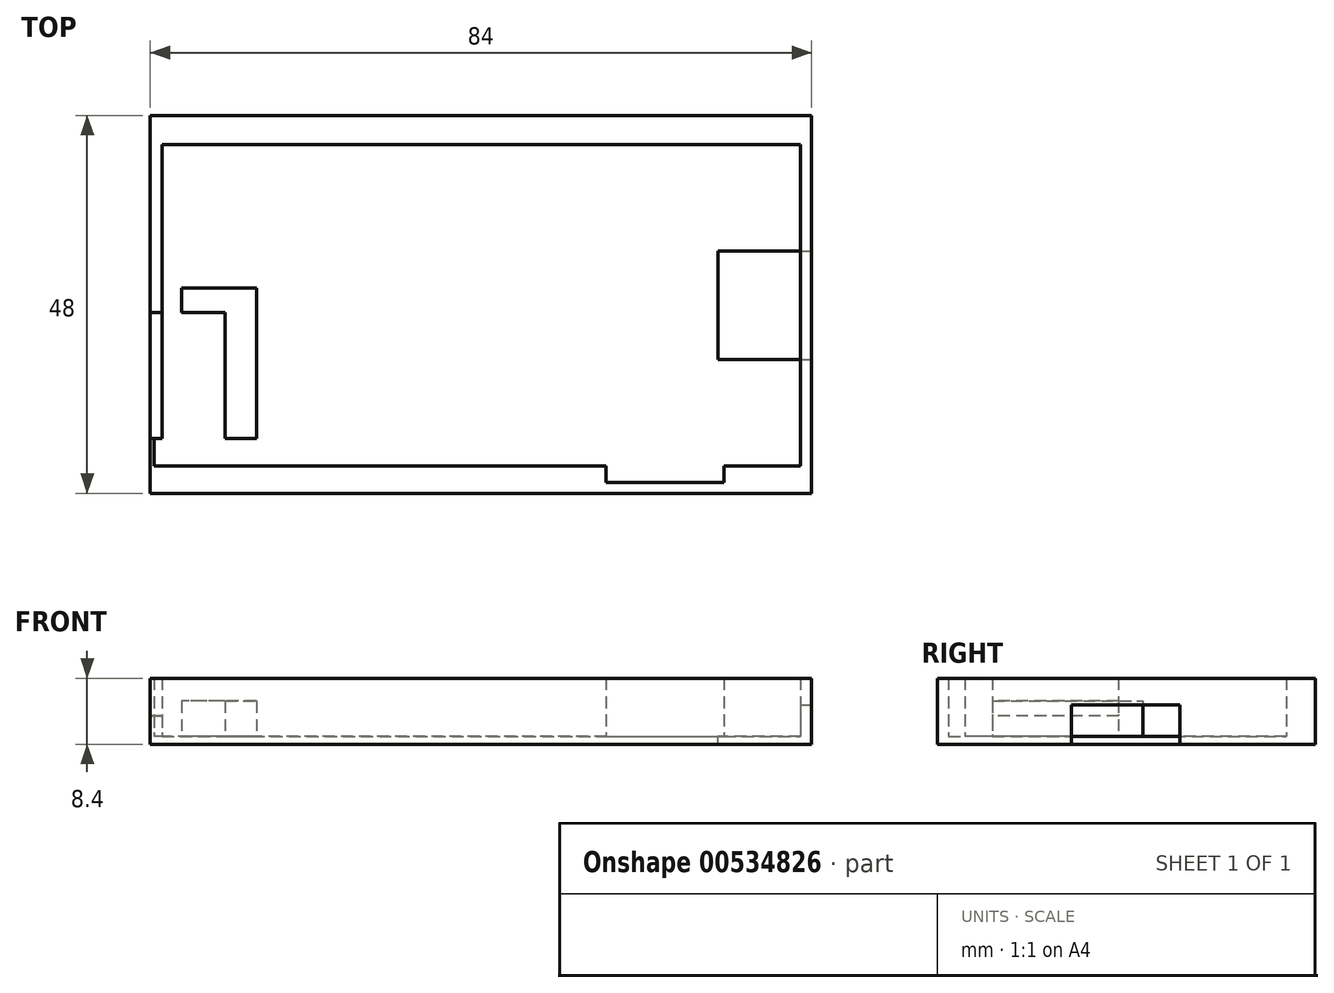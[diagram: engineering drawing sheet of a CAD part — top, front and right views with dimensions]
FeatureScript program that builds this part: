
annotation { "Feature Type Name" : "Feature", "Feature Type Description" : "" }
export const myFeature = defineFeature(function(context is Context, id is Id, definition is map)
    precondition{}
    {
        {
            var Q0;
            Q0=qCreatedBy(makeId("Top.planeOp"),FACE);
            var sketch = newSketch(context, id + "F0", { "sketchPlane" : qUnion([Q0])});
            skLineSegment(sketch, "E0.0", {"start": v(-50.68, -41.57) * mm, "end": v(30.32, -41.57) * mm});
            skLineSegment(sketch, "E1.0", {"start": v(-50.68, 6.43) * mm, "end": v(30.32, 6.43) * mm});
            skLineSegment(sketch, "E2", {"start": v(-50.68, -1.57) * mm, "end": v(-50.68, 6.43) * mm});
            skLineSegment(sketch, "E3", {"start": v(-50.68, 6.43) * mm, "end": v(-50.68, 6.43) * mm});
            skLineSegment(sketch, "E4", {"start": v(-50.68, -41.57) * mm, "end": v(-50.68, -41.57) * mm});
            skLineSegment(sketch, "E5", {"start": v(-50.68, -35.57) * mm, "end": v(-50.68, -41.57) * mm});
            skLineSegment(sketch, "E6", {"start": v(30.32, -41.57) * mm, "end": v(33.32, -41.57) * mm});
            skLineSegment(sketch, "E7", {"start": v(30.32, 6.43) * mm, "end": v(33.32, 6.43) * mm});
            skLineSegment(sketch, "E8", {"start": v(9.72, -37.67) * mm, "end": v(19.72, -37.67) * mm});
            skLineSegment(sketch, "E9", {"start": v(19.72, -37.67) * mm, "end": v(19.72, -35.57) * mm});
            skLineSegment(sketch, "E10", {"start": v(9.72, -37.67) * mm, "end": v(9.72, -35.67) * mm});
            skLineSegment(sketch, "E11", {"start": v(29.42, -34.57) * mm, "end": v(33.32, -34.57) * mm});
            skLineSegment(sketch, "E12", {"start": v(29.42, -26.07) * mm, "end": v(33.32, -26.07) * mm});
            skLineSegment(sketch, "E13", {"start": v(-46.68, -34.57) * mm, "end": v(-50.68, -34.57) * mm});
            skLineSegment(sketch, "E14", {"start": v(-50.68, -18.57) * mm, "end": v(-46.68, -18.57) * mm});
            skLineSegment(sketch, "E15", {"start": v(-46.68, 0.23) * mm, "end": v(29.42, 0.23) * mm});
            skLineSegment(sketch, "E16", {"start": v(-50.68, -18.57) * mm, "end": v(-50.68, 6.43) * mm});
            skLineSegment(sketch, "E17", {"start": v(-50.68, -34.57) * mm, "end": v(-50.68, -41.57) * mm});
            skLineSegment(sketch, "E18", {"start": v(33.32, 6.43) * mm, "end": v(33.32, -26.07) * mm});
            skLineSegment(sketch, "E19", {"start": v(33.32, -34.57) * mm, "end": v(33.32, -41.57) * mm});
            skLineSegment(sketch, "E20", {"start": v(29.42, -34.57) * mm, "end": v(29.42, -35.57) * mm});
            skLineSegment(sketch, "E21", {"start": v(-46.68, -34.57) * mm, "end": v(-46.68, -35.67) * mm});
            skLineSegment(sketch, "E22", {"start": v(-46.68, -18.57) * mm, "end": v(-46.68, 0.23) * mm});
            skLineSegment(sketch, "E23", {"start": v(29.42, 0.23) * mm, "end": v(29.42, -26.07) * mm});
            skLineSegment(sketch, "E24.0", {"start": v(31.92, 2.73) * mm, "end": v(31.92, -25.77) * mm});
            skLineSegment(sketch, "E24.1", {"start": v(-49.18, 2.73) * mm, "end": v(31.92, 2.73) * mm});
            skLineSegment(sketch, "E24.2", {"start": v(-49.18, -18.57) * mm, "end": v(-49.18, 2.73) * mm});
            skLineSegment(sketch, "E25", {"start": v(29.42, -35.57) * mm, "end": v(19.72, -35.57) * mm});
            skLineSegment(sketch, "E26", {"start": v(9.72, -35.67) * mm, "end": v(-46.68, -35.67) * mm});
            skLineSegment(sketch, "E27.0", {"start": v(29.42, -38.07) * mm, "end": v(22.22, -38.07) * mm});
            skLineSegment(sketch, "E27.1", {"start": v(7.22, -38.07) * mm, "end": v(-46.68, -38.07) * mm});
            skLineSegment(sketch, "E27.2", {"start": v(7.22, -40.17) * mm, "end": v(7.22, -38.07) * mm});
            skLineSegment(sketch, "E27.3", {"start": v(7.22, -40.17) * mm, "end": v(22.22, -40.17) * mm});
            skLineSegment(sketch, "E27.4", {"start": v(22.22, -40.17) * mm, "end": v(22.22, -38.07) * mm});
            skLineSegment(sketch, "E28", {"start": v(29.42, -38.07) * mm, "end": v(33.32, -38.07) * mm});
            skLineSegment(sketch, "E29", {"start": v(-46.68, -38.07) * mm, "end": v(-50.68, -38.07) * mm});
            skLineSegment(sketch, "E30", {"start": v(33.32, 6.43) * mm, "end": v(33.32, -41.57) * mm});
            skLineSegment(sketch, "E31", {"start": v(-50.68, 6.43) * mm, "end": v(-50.68, -41.57) * mm});
            skLineSegment(sketch, "E32", {"start": v(29.42, -24.57) * mm, "end": v(21.42, -24.57) * mm});
            skLineSegment(sketch, "E33", {"start": v(29.42, -12.77) * mm, "end": v(21.42, -12.77) * mm});
            skLineSegment(sketch, "E34", {"start": v(21.42, -12.77) * mm, "end": v(21.42, -24.57) * mm});
            skLineSegment(sketch, "E35", {"start": v(59.8, 40.02) * mm, "end": v(59.8, -75.73) * mm});
            skLineSegment(sketch, "E36", {"start": v(31.92, -25.77) * mm, "end": v(31.92, -34.57) * mm});
            skPoint(sketch, "E36.endSnap0", {"position": v(31.37, -34.57) * mm});
            skLineSegment(sketch, "E37", {"start": v(31.92, -34.57) * mm, "end": v(31.92, -38.07) * mm});
            skLineSegment(sketch, "E38", {"start": v(-46.68, -35.67) * mm, "end": v(-46.68, -38.07) * mm});
            skLineSegment(sketch, "E39", {"start": v(-50.18, -34.57) * mm, "end": v(-50.18, -38.07) * mm});
            skLineSegment(sketch, "E40", {"start": v(-49.18, -18.57) * mm, "end": v(-49.18, -34.57) * mm});
            skLineSegment(sketch, "E41", {"start": v(-41.18, -18.57) * mm, "end": v(-41.18, -34.57) * mm});
            skLineSegment(sketch, "E42", {"start": v(-37.18, -34.57) * mm, "end": v(-37.18, -18.57) * mm});
            skLineSegment(sketch, "E43", {"start": v(-41.18, -18.57) * mm, "end": v(-37.18, -18.57) * mm});
            skLineSegment(sketch, "E44", {"start": v(-41.18, -34.57) * mm, "end": v(-37.18, -34.57) * mm});
            skLineSegment(sketch, "E45", {"start": v(-37.18, -18.57) * mm, "end": v(-37.18, -15.51) * mm});
            skLineSegment(sketch, "E46", {"start": v(-37.18, -15.51) * mm, "end": v(-46.68, -15.51) * mm});
            skLineSegment(sketch, "E47", {"start": v(-41.18, -18.57) * mm, "end": v(-46.68, -18.57) * mm});
            skLineSegment(sketch, "E48", {"start": v(29.42, -24.57) * mm, "end": v(33.32, -24.57) * mm});
            skLineSegment(sketch, "E49", {"start": v(29.42, -12.77) * mm, "end": v(33.32, -12.77) * mm});
            skLineSegment(sketch, "E50", {"start": v(29.42, -10.77) * mm, "end": v(21.42, -10.77) * mm});
            skLineSegment(sketch, "E51", {"start": v(21.42, -10.77) * mm, "end": v(21.42, -12.77) * mm});
            skLineSegment(sketch, "E52", {"start": v(29.42, -10.77) * mm, "end": v(33.32, -10.77) * mm});
            skSolve(sketch);
        }
        {
            var Q0;
            Q0=makeQuery(id+"F0.imprint","IMPRINT",FACE,{"disambiguationData":[TD([[makeQuery(id+"F0.imprint","IMPRINT",EDGE,{"derivedFrom":sQuery(id+"F0.wireOp",EDGE,"E8")}),1.0]])]});
            var Q1;
            Q1=makeQuery(id+"F0.imprint","IMPRINT",FACE,{"disambiguationData":[TD([[makeQuery(id+"F0.imprint","IMPRINT",EDGE,{"derivedFrom":sQuery(id+"F0.wireOp",EDGE,"E15")}),1.0]])]});
            var Q2;
            {var subQ9=sQuery(id+"F0.wireOp",EDGE,"E1.0");Q2=makeQuery(id+"F0.imprint","IMPRINT",FACE,{"disambiguationData":[TD([[makeQuery(id+"F0.imprint","IMPRINT",EDGE,{"derivedFrom":subQ9}),-1.0]])]});}
            var Q3;
            Q3=makeQuery(id+"F0.imprint","IMPRINT",FACE,{"disambiguationData":[TD([[makeQuery(id+"F0.imprint","IMPRINT",EDGE,{"derivedFrom":sQuery(id+"F0.wireOp",EDGE,"E8")}),-1.0]])]});
            var Q4;
            {var subQ4=sQuery(id+"F0.wireOp",EDGE,"E0.0");Q4=makeQuery(id+"F0.imprint","IMPRINT",FACE,{"disambiguationData":[TD([[makeQuery(id+"F0.imprint","IMPRINT",EDGE,{"derivedFrom":subQ4}),1.0]])]});}
            var Q5;
            {var subQ3=sQuery(id+"F0.wireOp",EDGE,"E36");Q5=makeQuery(id+"F0.imprint","IMPRINT",FACE,{"disambiguationData":[TD([[makeQuery(id+"F0.imprint","IMPRINT",EDGE,{"derivedFrom":subQ3}),1.0]])]});}
            var Q6;
            {var subQ3=sQuery(id+"F0.wireOp",EDGE,"E37");Q6=makeQuery(id+"F0.imprint","IMPRINT",FACE,{"disambiguationData":[TD([[makeQuery(id+"F0.imprint","IMPRINT",EDGE,{"derivedFrom":subQ3}),1.0]])]});}
            var Q7;
            {var subQ0=sQuery(id+"F0.wireOp",EDGE,"E13");Q7=makeQuery(id+"F0.imprint","IMPRINT",FACE,{"disambiguationData":[TD([[makeQuery(id+"F0.imprint","IMPRINT",EDGE,{"derivedFrom":subQ0}),-1.0]])]});}
            var Q8;
            {var subQ2=sQuery(id+"F0.wireOp",EDGE,"E13");Q8=makeQuery(id+"F0.imprint","IMPRINT",FACE,{"disambiguationData":[TD([[makeQuery(id+"F0.imprint","IMPRINT",EDGE,{"derivedFrom":subQ2}),1.0]])]});}
            var Q9;
            {var subQ3=sQuery(id+"F0.wireOp",EDGE,"E21");Q9=makeQuery(id+"F0.imprint","IMPRINT",FACE,{"disambiguationData":[TD([[makeQuery(id+"F0.imprint","IMPRINT",EDGE,{"derivedFrom":subQ3}),-1.0]])]});}
            var Q10;
            {var subQ3=sQuery(id+"F0.wireOp",EDGE,"E39");Q10=makeQuery(id+"F0.imprint","IMPRINT",FACE,{"disambiguationData":[TD([[makeQuery(id+"F0.imprint","IMPRINT",EDGE,{"derivedFrom":subQ3}),-1.0]])]});}
            var Q11;
            Q11=makeQuery(id+"F0.imprint","IMPRINT",FACE,{"disambiguationData":[TD([[makeQuery(id+"F0.imprint","IMPRINT",EDGE,{"derivedFrom":sQuery(id+"F0.wireOp",EDGE,"E41")}),1.0]])]});
            var Q12;
            Q12=makeQuery(id+"F0.imprint","IMPRINT",FACE,{"disambiguationData":[TD([[makeQuery(id+"F0.imprint","IMPRINT",EDGE,{"derivedFrom":sQuery(id+"F0.wireOp",EDGE,"E43")}),1.0]])]});
            var Q13;
            {var subQ0=sQuery(id+"F0.wireOp",EDGE,"E30");var subQ1=sQuery(id+"F0.wireOp",EDGE,"E12");var subQ2=makeQuery(id+"F0.imprint","INTERSECT",VERTEX,{"derivedFrom":[subQ1,subQ0]});Q13=makeQuery(id+"F0.imprint","IMPRINT",FACE,{"disambiguationData":[TD([[makeQuery(id+"F0.imprint","IMPRINT",EDGE,{"disambiguationData":[TD([[subQ2,1.0]])],"derivedFrom":subQ0}),-1.0]])]});}
            var Q14;
            {var subQ0=sQuery(id+"F0.wireOp",EDGE,"E23");var subQ1=sQuery(id+"F0.wireOp",EDGE,"E12");var subQ2=makeQuery(id+"F0.imprint","INTERSECT",VERTEX,{"derivedFrom":[subQ1,subQ0]});Q14=makeQuery(id+"F0.imprint","IMPRINT",FACE,{"disambiguationData":[TD([[makeQuery(id+"F0.imprint","IMPRINT",EDGE,{"disambiguationData":[TD([[subQ2,-1.0]])],"derivedFrom":subQ1}),1.0]])]});}
            var Q15;
            {var subQ4=sQuery(id+"F0.wireOp",EDGE,"E20");Q15=makeQuery(id+"F0.imprint","IMPRINT",FACE,{"disambiguationData":[TD([[makeQuery(id+"F0.imprint","IMPRINT",EDGE,{"derivedFrom":subQ4}),-1.0]])]});}
            var Q16;
            {var subQ8=sQuery(id+"F0.wireOp",EDGE,"E24.2");Q16=makeQuery(id+"F0.imprint","IMPRINT",FACE,{"disambiguationData":[TD([[makeQuery(id+"F0.imprint","IMPRINT",EDGE,{"derivedFrom":subQ8}),-1.0]])]});}
            extrude(context, id + "F1", {"entities" : qUnion([Q0, Q1, Q2, Q3, Q4, Q5, Q6, Q7, Q8, Q9, Q10, Q11, Q12, Q13, Q14, Q15, Q16]), "oppositeDirection" : true, "depth" : 1 * mm, "offsetDistance" : 25 * mm});
        }
        {
            var Q0;
            {var subQ3=sQuery(id+"F0.wireOp",EDGE,"KbTD920z-0UKZ-KzV2-GkzX-uQvUb1giLStP");Q0=makeQuery(id+"F0.imprint","IMPRINT",FACE,{"disambiguationData":[TD([[makeQuery(id+"F0.imprint","IMPRINT",EDGE,{"derivedFrom":subQ3}),1.0]])]});}
            var Q1;
            {var subQ5=sQuery(id+"F0.wireOp",EDGE,"E0.0");Q1=makeQuery(id+"F0.imprint","IMPRINT",FACE,{"disambiguationData":[TD([[makeQuery(id+"F0.imprint","IMPRINT",EDGE,{"derivedFrom":subQ5}),1.0]])]});}
            var Q2;
            {var subQ9=sQuery(id+"F0.wireOp",EDGE,"E1.0");Q2=makeQuery(id+"F0.imprint","IMPRINT",FACE,{"disambiguationData":[TD([[makeQuery(id+"F0.imprint","IMPRINT",EDGE,{"derivedFrom":subQ9}),-1.0]])]});}
            var Q3;
            {var subQ3=sQuery(id+"F0.wireOp",EDGE,"E36");Q3=makeQuery(id+"F0.imprint","IMPRINT",FACE,{"disambiguationData":[TD([[makeQuery(id+"F0.imprint","IMPRINT",EDGE,{"derivedFrom":subQ3}),1.0]])]});}
            var Q4;
            {var subQ1=sQuery(id+"F0.wireOp",EDGE,"E19");Q4=makeQuery(id+"F0.imprint","IMPRINT",FACE,{"disambiguationData":[TD([[makeQuery(id+"F0.imprint","IMPRINT",EDGE,{"derivedFrom":subQ1}),-1.0]])]});}
            var Q5;
            {var subQ3=sQuery(id+"F0.wireOp",EDGE,"E39");Q5=makeQuery(id+"F0.imprint","IMPRINT",FACE,{"disambiguationData":[TD([[makeQuery(id+"F0.imprint","IMPRINT",EDGE,{"derivedFrom":subQ3}),-1.0]])]});}
            var Q6;
            {var subQ0=sQuery(id+"F0.wireOp",EDGE,"E30");var subQ1=sQuery(id+"F0.wireOp",EDGE,"E12");var subQ2=makeQuery(id+"F0.imprint","INTERSECT",VERTEX,{"derivedFrom":[subQ1,subQ0]});Q6=makeQuery(id+"F0.imprint","IMPRINT",FACE,{"disambiguationData":[TD([[makeQuery(id+"F0.imprint","IMPRINT",EDGE,{"disambiguationData":[TD([[subQ2,1.0]])],"derivedFrom":subQ0}),-1.0]])]});}
            var Q7;
            {var subQ0=sQuery(id+"F0.wireOp",EDGE,"E49");var subQ1=sQuery(id+"F0.wireOp",EDGE,"E24.0");var subQ2=makeQuery(id+"F0.imprint","INTERSECT",VERTEX,{"derivedFrom":[subQ1,subQ0]});Q7=makeQuery(id+"F0.imprint","IMPRINT",FACE,{"disambiguationData":[TD([[makeQuery(id+"F0.imprint","IMPRINT",EDGE,{"disambiguationData":[TD([[subQ2,-1.0]])],"derivedFrom":subQ1}),1.0]])]});}
            var Q8;
            {var subQ0=sQuery(id+"F0.wireOp",EDGE,"E52");var subQ1=sQuery(id+"F0.wireOp",EDGE,"E24.0");var subQ2=makeQuery(id+"F0.imprint","INTERSECT",VERTEX,{"derivedFrom":[subQ1,subQ0]});Q8=makeQuery(id+"F0.imprint","IMPRINT",FACE,{"disambiguationData":[TD([[makeQuery(id+"F0.imprint","IMPRINT",EDGE,{"disambiguationData":[TD([[subQ2,-1.0]])],"derivedFrom":subQ1}),1.0]])]});}
            extrude(context, id + "F2", {"entities" : qUnion([Q0, Q1, Q2, Q3, Q4, Q5, Q6, Q7, Q8]), "operationType" : NewBodyOperationType.ADD, "depth" : 7.4 * mm, "offsetDistance" : 25 * mm});
        }
        {
            var Q0;
            {var subQ3=sQuery(id+"F0.wireOp",EDGE,"E40");Q0=makeQuery(id+"F0.imprint","IMPRINT",FACE,{"disambiguationData":[TD([[makeQuery(id+"F0.imprint","IMPRINT",EDGE,{"derivedFrom":subQ3}),-1.0]])]});}
            extrude(context, id + "F3", {"entities" : qUnion([Q0]), "operationType" : NewBodyOperationType.ADD, "depth" : 2.6 * mm, "offsetDistance" : 25 * mm});
        }
        {
            var Q0;
            Q0=makeQuery(id+"F0.imprint","IMPRINT",FACE,{"disambiguationData":[TD([[makeQuery(id+"F0.imprint","IMPRINT",EDGE,{"derivedFrom":sQuery(id+"F0.wireOp",EDGE,"E41")}),1.0]])]});
            var Q1;
            Q1=makeQuery(id+"F0.imprint","IMPRINT",FACE,{"disambiguationData":[TD([[makeQuery(id+"F0.imprint","IMPRINT",EDGE,{"derivedFrom":sQuery(id+"F0.wireOp",EDGE,"E43")}),1.0]])]});
            extrude(context, id + "F4", {"entities" : qUnion([Q0, Q1]), "operationType" : NewBodyOperationType.ADD, "depth" : 4.5 * mm, "offsetDistance" : 25 * mm});
        }
        {
            var Q0;
            {var subQ0=sQuery(id+"F0.wireOp",EDGE,"E49");var subQ1=sQuery(id+"F0.wireOp",EDGE,"E24.0");var subQ2=makeQuery(id+"F0.imprint","INTERSECT",VERTEX,{"derivedFrom":[subQ1,subQ0]});Q0=makeQuery(id+"F0.imprint","IMPRINT",FACE,{"disambiguationData":[TD([[makeQuery(id+"F0.imprint","IMPRINT",EDGE,{"disambiguationData":[TD([[subQ2,-1.0]])],"derivedFrom":subQ1}),1.0]])]});}
            var Q1;
            {var subQ0=sQuery(id+"F0.wireOp",EDGE,"E52");var subQ1=sQuery(id+"F0.wireOp",EDGE,"E24.0");var subQ2=makeQuery(id+"F0.imprint","INTERSECT",VERTEX,{"derivedFrom":[subQ1,subQ0]});Q1=makeQuery(id+"F0.imprint","IMPRINT",FACE,{"disambiguationData":[TD([[makeQuery(id+"F0.imprint","IMPRINT",EDGE,{"disambiguationData":[TD([[subQ2,-1.0]])],"derivedFrom":subQ1}),1.0]])]});}
            extrude(context, id + "F5", {"entities" : qUnion([Q0, Q1]), "operationType" : NewBodyOperationType.REMOVE, "depth" : 4 * mm, "offsetDistance" : 25 * mm});
        }
    });
